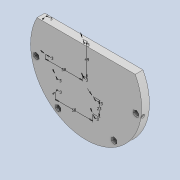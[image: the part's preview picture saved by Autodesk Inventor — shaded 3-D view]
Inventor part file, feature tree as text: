
AUTODESK INVENTOR PART (.ipt)
format: ipt  version: 2020.4 (Build 244396000, 396)  size: 243,200 bytes
history: native  units: mm
features: sketch x11, extrude x10, projected_geometry x5, plane x4
ambient origin geometry x8: Origin, YZ Plane, XZ Plane, XY Plane, X Axis, Y Axis, Z Axis, Center Point
bodies: Solid1 (feature_tree)
feature tree (30):
  extrude  "Extrusion1"  Depth=78.0mm
  extrude  "Extrusion2"  Depth=12.0mm
  extrude  "Extrusion3"  Depth=4.22mm
  extrude  "Extrusion4"  Depth=20.0mm
  extrude  "Extrusion5"  Depth=40.0mm
  extrude  "Extrusion6"  Depth=4.0mm TaperAngle=0.0deg
  plane  "Work Plane1"
  extrude  "Extrusion7"  Depth=5.0mm
  plane  "Work Plane2"
  extrude  "Extrusion8"  Depth=5.0mm TaperAngle=0.0deg
  plane  "Work Plane3"
  extrude  "Extrusion9"  Depth=5.0mm
  plane  "Work Plane4"
  extrude  "Extrusion10"  Depth=5.0mm TaperAngle=0.0deg
  sketch  "Sketch11"  dims[d35=3.0mm d36=2.436418mm d37=5.0mm d38=5.0mm d39=0.0mm d40=3.0mm d41=2.436418mm d42=5.0mm d43=5.0mm d44=0.0mm d45=-2.0mm d46=5.5mm d47=10.0mm d48=0.0mm d49=-2.0mm d50=5.5mm d51=10.0mm d52=0.0mm d53=-2.0mm d54=5.5mm d55=10.0mm d56=0.0mm d57=-2.0mm d58=5.5mm d59=10.0mm d60=0.0mm d69=58.0mm d70=49.0mm d71=3.0mm d72=3.0mm d73=3.0mm d74=3.0mm d75=58.0mm d76=23.0mm d77=3.0mm d78=3.0mm d79=3.0mm d80=3.0mm]
  sketch  "Sketch1"  dims[d0=171.6mm d1=78.0mm]
  sketch  "Sketch2"  dims[d2=78.0mm d5=12.0mm]
  projected_geometry  "Projected Loop1"
  sketch  "Sketch3"  dims[d6=4.22mm d7=4.22mm]
  projected_geometry  "Projected Loop2"
  sketch  "Sketch4"  dims[d10=12.0mm d11=20.0mm d13=8.290314mm]
  projected_geometry  "Projected Loop3"
  sketch  "Sketch5"  dims[d15=20.0mm d17=8.290314mm d19=40.0mm]
  projected_geometry  "Projected Loop4"
  sketch  "Sketch6"  dims[d20=12.0mm d21=0.0mm d22=4.0mm d23=0.0mm]
  projected_geometry  "Projected Loop5"
  sketch  "Sketch7"  dims[d24=3.0mm d26=5.0mm]
  sketch  "Sketch8"  dims[d27=2.436418mm d28=5.0mm d29=0.0mm]
  sketch  "Sketch9"  dims[d30=3.0mm d31=5.0mm]
  sketch  "Sketch10"  dims[d32=2.436418mm d33=5.0mm d34=0.0mm]
